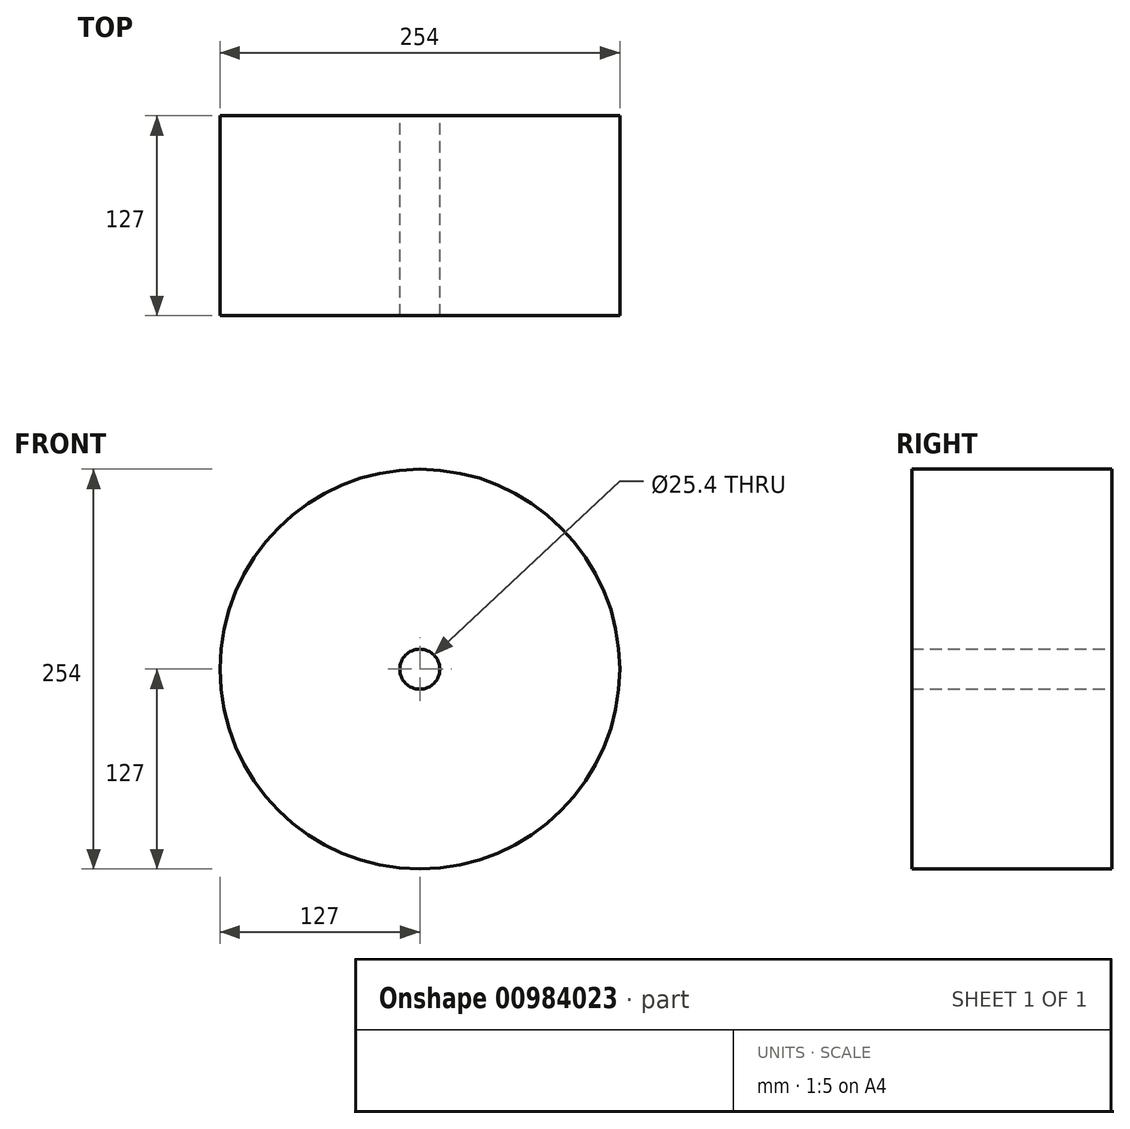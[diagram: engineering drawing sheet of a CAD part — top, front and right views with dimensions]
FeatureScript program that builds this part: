
annotation { "Feature Type Name" : "Feature", "Feature Type Description" : "" }
export const myFeature = defineFeature(function(context is Context, id is Id, definition is map)
    precondition{}
    {
        {
            var Q0;
            Q0=qCreatedBy(makeId("Front.planeOp"),FACE);
            var sketch = newSketch(context, id + "F0", { "sketchPlane" : qUnion([Q0])});
            skCircle(sketch, "E0", {"center": v(0, 0) * mm, "radius": 127 * mm});
            skCircle(sketch, "E1", {"center": v(0, 0) * mm, "radius": 12.7 * mm});
            skSolve(sketch);
        }
        {
            var Q0;
            Q0 = qSketchRegion(id + "F0", true);
            extrude(context, id + "F1", {"entities" : qUnion([Q0]), "depth" : 127 * mm, "offsetDistance" : 25.4 * mm});
        }
    });
